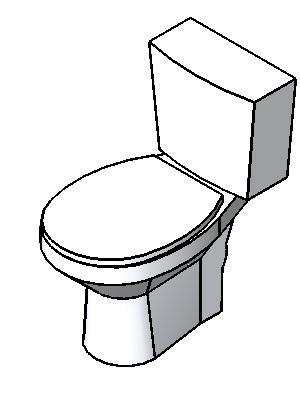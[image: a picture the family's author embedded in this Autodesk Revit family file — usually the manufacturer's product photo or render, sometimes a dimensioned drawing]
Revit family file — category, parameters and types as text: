
# Revit family: Deca_Bacia convencional suspensa_Quadra_P.213
name_source: partatom
category: Plumbing Fixtures
units: mm (PartAtom-declared; Revit-internal decimal feet)

## family parameters
Cut with Voids When Loaded = No
Host = Face
Part Type = Normal
Room Calculation Point = No
Round Connector Dimension = Use Radius
Shared = No

## types (1)
- P.213.17_Branco
    Acompanha o Produto = Conexão de entrada de água para Bacia convencional + Acabamento para fixação (SBS.01.17)
    Aprovado por = quattroD
    Atendimento ao Cliente = 0800-0117073
    CWFU = 0
    Categoria = BACIAS E BIDES
    Composição Anel Vedação = Não Possui
    Composição Assento = -
    Composição Básica = Argila, feldspato, caulim, vidrados e corantes inorgânicos.
    Composição Componente = Liga de elastômeros e plásticos de engenharia.
    Consumo = 6 lpf
    Cor Interna = -
    Cor Principal = Branco
    Cor Secundária = -
    Cores Componente = -
    Criado por = quattroD
    Código Pai = P.213
    Default Elevation = 0 m
    Description = Bacia convencional suspensa
    Diâmetro Ponto de Esgoto = 0.1 m
    Diâmetro Água Fria = 0.04 m
    Informações Complementares = -
    Itens de Instalação = SP.132.01
    Linha = Quadra
    Manufacturer = Deca
    Material = Deca_Branco
    Model = P.213.17
    Norma = NBR-16727-1;NBR-16727-2
    Peso Líquido (Kg) = 22.897
    Pressão máx. funcionamento = -
    Pressão mín. Aquec. Acúmulo = -
    Pressão mín. Aquec. Passagem = -
    Pressão mín. funcionamento = -
    Raio Ponto de Esgoto = 0.05 m
    Raio Água Fria = 0.02 m
    Saída de Esgoto = Saída de Esgoto Horizontal
    Segmento = Banheiro Médio
    Tipo de dispositivo economizador = -
    Tipo de mecanismo utilizado = -
    Tipo de rosca de entrada = -
    Tipo de rosca de saída = -
    URL = www.deca.com.br
    Vazão na Pressão máx. (L/min) = -
    Vazão na Pressão mín. (L/min) = -
    WFU = 0

## geometry (parser evidence)
native form markers: Sweep x2
no freeform markers — native parametric forms only
